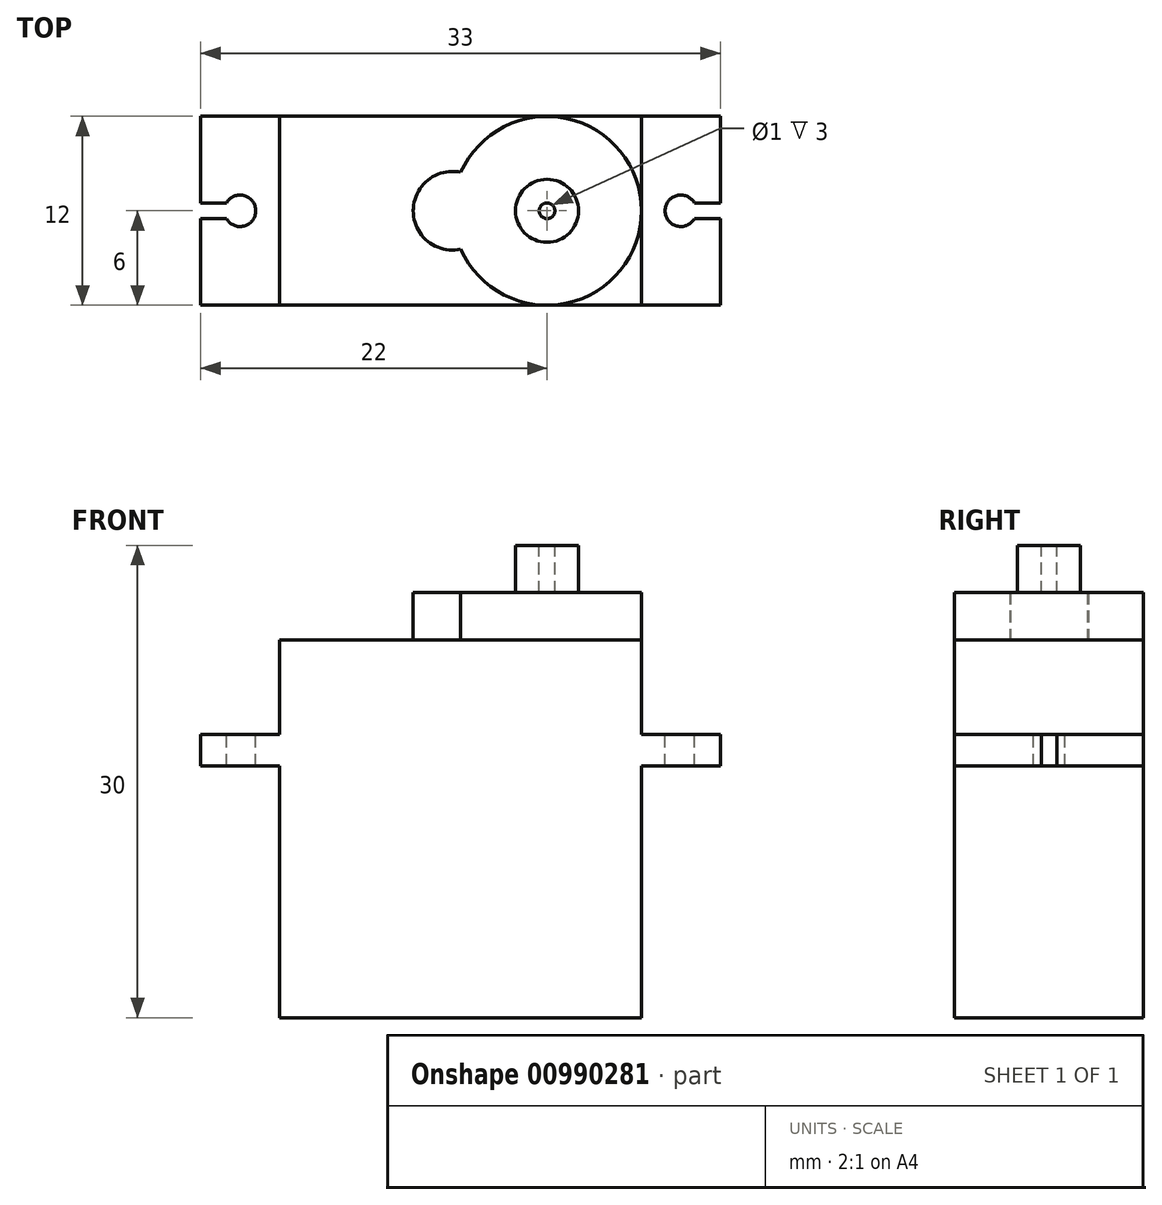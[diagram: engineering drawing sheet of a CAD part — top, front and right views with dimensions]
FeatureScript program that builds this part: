
annotation { "Feature Type Name" : "Feature", "Feature Type Description" : "" }
export const myFeature = defineFeature(function(context is Context, id is Id, definition is map)
    precondition{}
    {
        {
            var Q0;
            Q0=qCreatedBy(makeId("Top.planeOp"),FACE);
            var sketch = newSketch(context, id + "F0", { "sketchPlane" : qUnion([Q0])});
            skLineSegment(sketch, "E0.bottom", {"start": v(11.5, 6) * mm, "end": v(-11.5, 6) * mm});
            skLineSegment(sketch, "E0.top", {"start": v(11.5, -6) * mm, "end": v(-11.5, -6) * mm});
            skLineSegment(sketch, "E0.left", {"start": v(11.5, 6) * mm, "end": v(11.5, -6) * mm});
            skLineSegment(sketch, "E0.right", {"start": v(-11.5, 6) * mm, "end": v(-11.5, -6) * mm});
            skPoint(sketch, "E0.middle", {"position": v(0, 0) * mm});
            skSolve(sketch);
        }
        {
            var Q0;
            Q0=qSketchRegion(id+"F0",true);
            extrude(context, id + "F1", {"entities" : qUnion([Q0]), "depth" : 16 * mm, "offsetDistance" : 25 * mm});
        }
        {
            var Q0;
            Q0=makeQuery(id+"F1.opExtrude","CAP_FACE",FACE,{"disambiguationData":[OSD([sQuery(id+"F0.wireOp",EDGE,"E0.bottom"),sQuery(id+"F0.wireOp",EDGE,"E0.top"),sQuery(id+"F0.wireOp",EDGE,"E0.left"),sQuery(id+"F0.wireOp",EDGE,"E0.right")])],"isStart":false});
            var sketch = newSketch(context, id + "F2", { "sketchPlane" : qUnion([Q0])});
            skLineSegment(sketch, "E1.bottom", {"start": v(-16.5, 6) * mm, "end": v(16.5, 6) * mm});
            skLineSegment(sketch, "E1.top", {"start": v(-16.5, -6) * mm, "end": v(16.5, -6) * mm});
            skLineSegment(sketch, "E1.left", {"start": v(-16.5, 6) * mm, "end": v(-16.5, -6) * mm});
            skLineSegment(sketch, "E1.right", {"start": v(16.5, 6) * mm, "end": v(16.5, -6) * mm});
            skPoint(sketch, "E1.middle", {"position": v(0, 0) * mm});
            skSolve(sketch);
        }
        {
            var Q0;
            Q0=qSketchRegion(id+"F2",true);
            extrude(context, id + "F3", {"entities" : qUnion([Q0]), "operationType" : NewBodyOperationType.ADD, "depth" : 2 * mm, "offsetDistance" : 25 * mm});
        }
        {
            var Q0;
            Q0=makeQuery(id+"F3.opExtrude","CAP_FACE",FACE,{"disambiguationData":[OSD([sQuery(id+"F2.wireOp",EDGE,"E1.bottom"),sQuery(id+"F2.wireOp",EDGE,"E1.top"),sQuery(id+"F2.wireOp",EDGE,"E1.left"),sQuery(id+"F2.wireOp",EDGE,"E1.right")])],"isStart":false});
            var sketch = newSketch(context, id + "F4", { "sketchPlane" : qUnion([Q0])});
            skLineSegment(sketch, "E2.bottom", {"start": v(11.5, 6) * mm, "end": v(-11.5, 6) * mm});
            skLineSegment(sketch, "E2.top", {"start": v(11.5, -6) * mm, "end": v(-11.5, -6) * mm});
            skLineSegment(sketch, "E2.left", {"start": v(11.5, 6) * mm, "end": v(11.5, -6) * mm});
            skLineSegment(sketch, "E2.right", {"start": v(-11.5, 6) * mm, "end": v(-11.5, -6) * mm});
            skPoint(sketch, "E2.middle", {"position": v(0, 0) * mm});
            skSolve(sketch);
        }
        {
            var Q0;
            Q0=qSketchRegion(id+"F4",true);
            extrude(context, id + "F5", {"entities" : qUnion([Q0]), "operationType" : NewBodyOperationType.ADD, "depth" : 6 * mm, "offsetDistance" : 25 * mm});
        }
        {
            var Q0;
            Q0=makeQuery(id+"F5.opExtrude","CAP_FACE",FACE,{"disambiguationData":[OSD([sQuery(id+"F4.wireOp",EDGE,"E2.bottom"),sQuery(id+"F4.wireOp",EDGE,"E2.top"),sQuery(id+"F4.wireOp",EDGE,"E2.left"),sQuery(id+"F4.wireOp",EDGE,"E2.right")])],"isStart":false});
            var sketch = newSketch(context, id + "F6", { "sketchPlane" : qUnion([Q0])});
            skCircle(sketch, "E3", {"center": v(5.5, 0) * mm, "radius": 6 * mm});
            skCircle(sketch, "E4", {"center": v(-0.5, 0) * mm, "radius": 2.5 * mm});
            skSolve(sketch);
        }
        {
            var Q0;
            Q0=qSketchRegion(id+"F6",true);
            extrude(context, id + "F7", {"entities" : qUnion([Q0]), "operationType" : NewBodyOperationType.ADD, "depth" : 3 * mm, "offsetDistance" : 25 * mm});
        }
        {
            var Q0;
            Q0=makeQuery(id+"F7.opExtrude","CAP_FACE",FACE,{"disambiguationData":[OSD([sQuery(id+"F6.wireOp",EDGE,"E3"),sQuery(id+"F6.wireOp",EDGE,"E4")])],"isStart":false});
            var sketch = newSketch(context, id + "F8", { "sketchPlane" : qUnion([Q0])});
            skCircle(sketch, "E5", {"center": v(5.5, 0) * mm, "radius": 2 * mm});
            skSolve(sketch);
        }
        {
            var Q0;
            Q0=qSketchRegion(id+"F8",true);
            extrude(context, id + "F9", {"entities" : qUnion([Q0]), "operationType" : NewBodyOperationType.ADD, "depth" : 3 * mm, "offsetDistance" : 25 * mm});
        }
        {
            var Q0;
            {var subQ0=sQuery(id+"F2.wireOp",EDGE,"E1.top");var subQ1=sQuery(id+"F2.wireOp",EDGE,"E1.bottom");var subQ2=sQuery(id+"F2.wireOp",EDGE,"E1.left");Q0=makeQuery(id+"F5.boolean.opBoolean","SPLIT",FACE,{"disambiguationData":[TD([makeQuery(id+"F3.opExtrude","SWEPT_FACE",FACE,{"disambiguationData":[OSD([subQ2])]})])],"derivedFrom":makeQuery(id+"F3.opExtrude","CAP_FACE",FACE,{"disambiguationData":[OSD([subQ1,subQ0,subQ2,sQuery(id+"F2.wireOp",EDGE,"E1.right")])],"isStart":false})});}
            var sketch = newSketch(context, id + "F10", { "sketchPlane" : qUnion([Q0])});
            skCircle(sketch, "E6", {"center": v(-14, 0) * mm, "radius": 1 * mm});
            skCircle(sketch, "E7", {"center": v(14, 0) * mm, "radius": 1 * mm});
            skLineSegment(sketch, "E8.bottom", {"start": v(-16.5, -0.5) * mm, "end": v(-14.87, -0.5) * mm});
            skLineSegment(sketch, "E8.top", {"start": v(-16.5, 0.5) * mm, "end": v(-14.87, 0.5) * mm});
            skLineSegment(sketch, "E8.left", {"start": v(-16.5, -0.5) * mm, "end": v(-16.5, 0.5) * mm});
            skLineSegment(sketch, "E8.right", {"start": v(-14.87, -0.5) * mm, "end": v(-14.87, 0.5) * mm});
            skLineSegment(sketch, "E9.bottom", {"start": v(14.87, 0.5) * mm, "end": v(16.5, 0.5) * mm});
            skLineSegment(sketch, "E9.top", {"start": v(14.87, -0.5) * mm, "end": v(16.5, -0.5) * mm});
            skLineSegment(sketch, "E9.left", {"start": v(14.87, 0.5) * mm, "end": v(14.87, -0.5) * mm});
            skLineSegment(sketch, "E9.right", {"start": v(16.5, 0.5) * mm, "end": v(16.5, -0.5) * mm});
            skSolve(sketch);
        }
        {
            var Q0;
            Q0=qSketchRegion(id+"F10",true);
            extrude(context, id + "F11", {"entities" : qUnion([Q0]), "operationType" : NewBodyOperationType.REMOVE, "endBound" : BoundingType.THROUGH_ALL, "oppositeDirection" : true, "depth" : 25 * mm, "offsetDistance" : 25 * mm});
        }
        {
            var Q0;
            Q0=makeQuery(id+"F9.opExtrude","CAP_FACE",FACE,{"disambiguationData":[OSD([sQuery(id+"F8.wireOp",EDGE,"E5")])],"isStart":false});
            var sketch = newSketch(context, id + "F12", { "sketchPlane" : qUnion([Q0])});
            skCircle(sketch, "E10", {"center": v(5.5, 0) * mm, "radius": 0.5 * mm});
            skSolve(sketch);
        }
        {
            var Q0;
            Q0=qSketchRegion(id+"F12",true);
            extrude(context, id + "F13", {"entities" : qUnion([Q0]), "operationType" : NewBodyOperationType.REMOVE, "oppositeDirection" : true, "depth" : 3 * mm, "offsetDistance" : 25 * mm});
        }
    });
